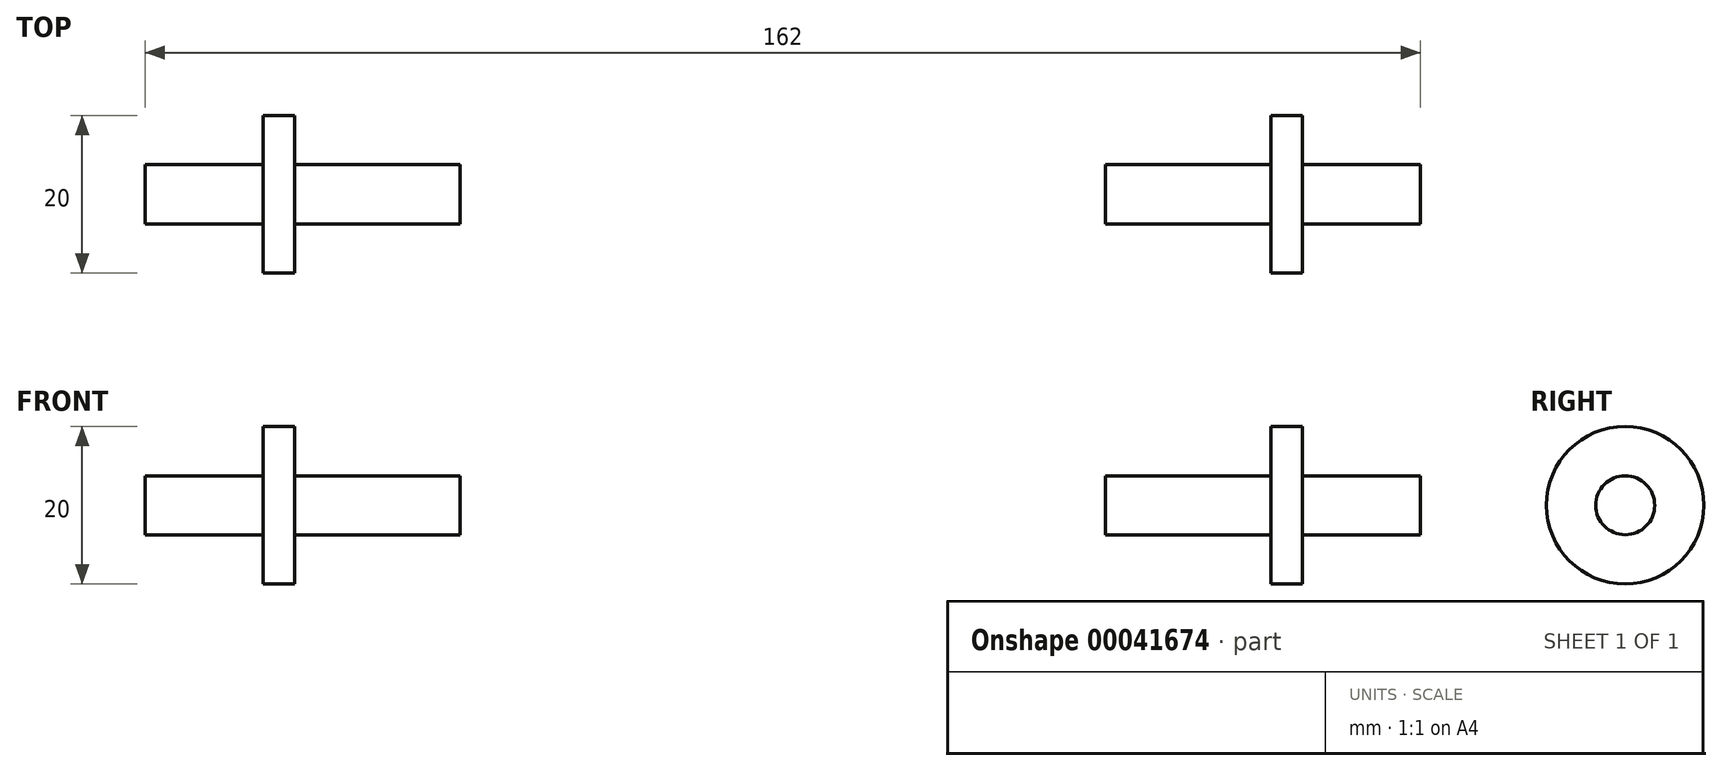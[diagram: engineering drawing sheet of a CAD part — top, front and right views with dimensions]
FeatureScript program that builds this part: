
annotation { "Feature Type Name" : "Feature", "Feature Type Description" : "" }
export const myFeature = defineFeature(function(context is Context, id is Id, definition is map)
    precondition{}
    {
        {
            var Q0;
            Q0=qCreatedBy(makeId("Top.planeOp"),FACE);
            var sketch = newSketch(context, id + "F0", { "sketchPlane" : qUnion([Q0])});
            skLineSegment(sketch, "E0", {"start": v(0, 0) * mm, "end": v(41, 0) * mm, "construction": true});
            skLineSegment(sketch, "E1.bottom", {"start": v(41, 0) * mm, "end": v(62, 0) * mm});
            skLineSegment(sketch, "E1.top", {"start": v(41, 3.75) * mm, "end": v(62, 3.75) * mm});
            skLineSegment(sketch, "E1.left", {"start": v(41, 0) * mm, "end": v(41, 3.75) * mm});
            skLineSegment(sketch, "E1.right", {"start": v(62, 0) * mm, "end": v(62, 3.75) * mm});
            skLineSegment(sketch, "E2", {"start": v(62, 3.75) * mm, "end": v(62, 10) * mm});
            skLineSegment(sketch, "E3", {"start": v(62, 10) * mm, "end": v(66, 10) * mm});
            skLineSegment(sketch, "E4", {"start": v(66, 10) * mm, "end": v(66, 0) * mm});
            skLineSegment(sketch, "E5", {"start": v(66, 0) * mm, "end": v(62, 0) * mm});
            skLineSegment(sketch, "E6", {"start": v(66, 0) * mm, "end": v(81, 0) * mm});
            skLineSegment(sketch, "E7", {"start": v(81, 0) * mm, "end": v(81, 3.75) * mm});
            skLineSegment(sketch, "E8", {"start": v(81, 3.75) * mm, "end": v(66, 3.75) * mm});
            skSolve(sketch);
        }
        {
            var Q0;
            Q0=makeQuery(id+"F0.imprint","IMPRINT",FACE,{"disambiguationData":[TD([[makeQuery(id+"F0.imprint","IMPRINT",EDGE,{"derivedFrom":sQuery(id+"F0.wireOp",EDGE,"E1.bottom")}),1.0]])]});
            var Q1;
            {var subQ1=sQuery(id+"F0.wireOp",EDGE,"E6");Q1=makeQuery(id+"F0.imprint","IMPRINT",FACE,{"disambiguationData":[TD([[makeQuery(id+"F0.imprint","IMPRINT",EDGE,{"derivedFrom":subQ1}),1.0]])]});}
            var Q2;
            Q2=makeQuery(id+"F0.imprint","IMPRINT",FACE,{"disambiguationData":[TD([[makeQuery(id+"F0.imprint","IMPRINT",EDGE,{"derivedFrom":sQuery(id+"F0.wireOp",EDGE,"E1.right")}),-1.0]])]});
            var Q3;
            Q3=sQuery(id+"F0.wireOp",EDGE,"E1.bottom");
            revolve(context, id + "F1", {"entities" : qUnion([Q0, Q1, Q2]), "axis" : qUnion([Q3]), "revolveType" : RevolveType.FULL});
        }
        {
            var Q0;
            Q0=makeQuery(id+"F1.opRevolve","SWEPT_BODY",BODY,{"disambiguationData":[OSD([sQuery(id+"F0.wireOp",EDGE,"E1.bottom"),sQuery(id+"F0.wireOp",EDGE,"E1.top"),sQuery(id+"F0.wireOp",EDGE,"E1.left"),sQuery(id+"F0.wireOp",EDGE,"E2"),sQuery(id+"F0.wireOp",EDGE,"E3"),sQuery(id+"F0.wireOp",EDGE,"E4"),sQuery(id+"F0.wireOp",EDGE,"E5"),sQuery(id+"F0.wireOp",EDGE,"E6"),sQuery(id+"F0.wireOp",EDGE,"E7"),sQuery(id+"F0.wireOp",EDGE,"E8")])]});
            var Q1;
            Q1=qCreatedBy(makeId("Right.planeOp"),FACE);
            mirror(context, id + "F2", {"entities" : qUnion([Q0]), "mirrorPlane" : qUnion([Q1])});
        }
    });
